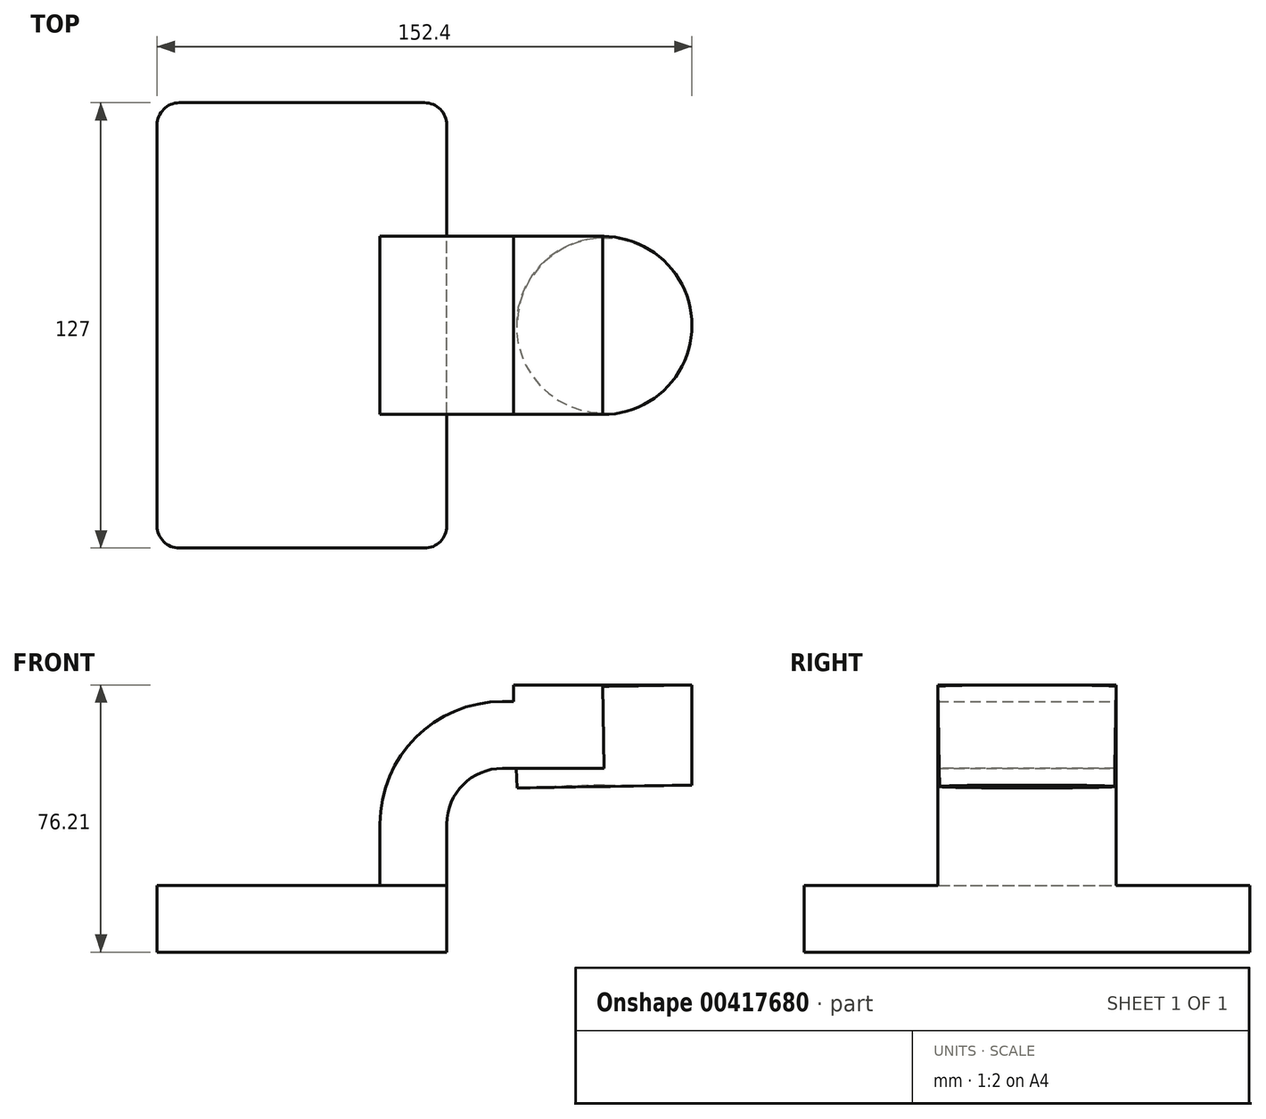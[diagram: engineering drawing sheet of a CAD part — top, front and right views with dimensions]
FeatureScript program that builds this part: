
annotation { "Feature Type Name" : "Feature", "Feature Type Description" : "" }
export const myFeature = defineFeature(function(context is Context, id is Id, definition is map)
    precondition{}
    {
        {
            var Q0;
            Q0=qCreatedBy(makeId("Front.planeOp"),FACE);
            var sketch = newSketch(context, id + "F0", { "sketchPlane" : qUnion([Q0])});
            skLineSegment(sketch, "E0.bottom", {"start": v(41.28, -9.52) * mm, "end": v(-41.27, -9.53) * mm});
            skLineSegment(sketch, "E0.top", {"start": v(41.27, 9.53) * mm, "end": v(-41.28, 9.53) * mm});
            skLineSegment(sketch, "E0.left", {"start": v(41.28, -9.52) * mm, "end": v(41.28, 9.53) * mm});
            skLineSegment(sketch, "E0.right", {"start": v(-41.27, -9.53) * mm, "end": v(-41.28, 9.53) * mm});
            skPoint(sketch, "E0.middle", {"position": v(0, 0) * mm});
            skLineSegment(sketch, "E1.bottom", {"start": v(60.32, 38.1) * mm, "end": v(111.12, 38.1) * mm});
            skLineSegment(sketch, "E1.top", {"start": v(60.32, 66.68) * mm, "end": v(111.12, 66.68) * mm});
            skLineSegment(sketch, "E1.left", {"start": v(60.32, 38.1) * mm, "end": v(60.32, 66.67) * mm});
            skLineSegment(sketch, "E1.right", {"start": v(111.12, 38.1) * mm, "end": v(111.12, 66.67) * mm});
            skPoint(sketch, "E1.middle", {"position": v(85.72, 52.39) * mm});
            skLineSegment(sketch, "E2", {"start": v(41.27, 9.53) * mm, "end": v(41.27, 27) * mm});
            skArc(sketch, "E3", {"start": v(41.27, 27) * mm, "mid": v(45.92, 38.23) * mm, "end": v(57.15, 42.88) * mm});
            skLineSegment(sketch, "E4", {"start": v(57.15, 42.88) * mm, "end": v(86.2, 42.88) * mm});
            skLineSegment(sketch, "E5.0", {"start": v(57.15, 61.93) * mm, "end": v(85.72, 61.93) * mm});
            skArc(sketch, "E5.1", {"start": v(22.23, 27) * mm, "mid": v(32.45, 51.7) * mm, "end": v(57.15, 61.93) * mm});
            skLineSegment(sketch, "E5.2", {"start": v(22.22, 9.53) * mm, "end": v(22.22, 27) * mm});
            skPoint(sketch, "E6", {"position": v(85.72, 66.68) * mm});
            skLineSegment(sketch, "E7", {"start": v(85.72, 66.68) * mm, "end": v(86.2, 38.1) * mm});
            skFitSpline(sketch, "E8", {"points": [v(-41.28, 9.52) * mm, v(57.15, 61.93) * mm], "startDerivative": vector(0.7, 129.9) * mm, "endDerivative": vector(128.03, 0.11) * mm});
            skSolve(sketch);
        }
        {
            var Q0;
            Q0=makeQuery(id+"F0.imprint","IMPRINT",FACE,{"disambiguationData":[TD([[makeQuery(id+"F0.imprint","IMPRINT",EDGE,{"derivedFrom":sQuery(id+"F0.wireOp",EDGE,"E0.bottom")}),-1.0]])]});
            extrude(context, id + "F1", {"entities" : qUnion([Q0]), "endBound" : BoundingType.SYMMETRIC, "depth" : 127 * mm});
        }
        {
            var Q0;
            {var subQ1=sQuery(id+"F0.wireOp",EDGE,"E2");Q0=makeQuery(id+"F0.imprint","IMPRINT",FACE,{"disambiguationData":[TD([[makeQuery(id+"F0.imprint","IMPRINT",EDGE,{"derivedFrom":subQ1}),1.0]])]});}
            var Q1;
            {var subQ1=sQuery(id+"F0.wireOp",EDGE,"E1.left");var subQ5=sQuery(id+"F0.wireOp",EDGE,"E1.top");var subQ6=makeQuery(id+"F0.imprint","INTERSECT",VERTEX,{"derivedFrom":[subQ5,subQ1]});Q1=makeQuery(id+"F0.imprint","IMPRINT",FACE,{"disambiguationData":[TD([[makeQuery(id+"F0.imprint","IMPRINT",EDGE,{"disambiguationData":[TD([[subQ6,-1.0]])],"derivedFrom":subQ5}),-1.0]])]});}
            extrude(context, id + "F2", {"entities" : qUnion([Q0, Q1]), "operationType" : NewBodyOperationType.ADD, "endBound" : BoundingType.SYMMETRIC, "depth" : 50.8 * mm});
        }
        {
            var Q0;
            {var subQ4=sQuery(id+"F0.wireOp",EDGE,"E5.1");Q0=makeQuery(id+"F0.imprint","IMPRINT",FACE,{"disambiguationData":[TD([[makeQuery(id+"F0.imprint","IMPRINT",EDGE,{"derivedFrom":subQ4}),1.0]])]});}
            extrude(context, id + "F3", {"entities" : qUnion([Q0]), "operationType" : NewBodyOperationType.ADD, "endBound" : BoundingType.SYMMETRIC, "depth" : 15.88 * mm});
        }
        {
            var Q0;
            {var subQ4=sQuery(id+"F0.wireOp",EDGE,"E1.right");Q0=makeQuery(id+"F0.imprint","IMPRINT",FACE,{"disambiguationData":[TD([[makeQuery(id+"F0.imprint","IMPRINT",EDGE,{"derivedFrom":subQ4}),1.0]])]});}
            var Q1;
            Q1=sQuery(id+"F0.wireOp",EDGE,"E7");
            revolve(context, id + "F4", {"operationType" : NewBodyOperationType.ADD, "entities" : qUnion([Q0]), "axis" : qUnion([Q1]), "revolveType" : RevolveType.FULL});
        }
        {
            var Q0;
            Q0=makeQuery(id+"F1.opExtrude","CAP_EDGE",EDGE,{"disambiguationData":[OSD([sQuery(id+"F0.wireOp",EDGE,"E0.left")])],"isStart":false});
            var Q1;
            Q1=makeQuery(id+"F1.opExtrude","CAP_EDGE",EDGE,{"disambiguationData":[OSD([sQuery(id+"F0.wireOp",EDGE,"E0.right")])],"isStart":false});
            var Q2;
            Q2=makeQuery(id+"F1.opExtrude","CAP_EDGE",EDGE,{"disambiguationData":[OSD([sQuery(id+"F0.wireOp",EDGE,"E0.left")])],"isStart":true});
            var Q3;
            Q3=makeQuery(id+"F1.opExtrude","CAP_EDGE",EDGE,{"disambiguationData":[OSD([sQuery(id+"F0.wireOp",EDGE,"E0.right")])],"isStart":true});
            fillet(context, id + "F5", {"entities" : qUnion([Q0, Q1, Q2, Q3]), "radius" : 6.35 * mm, "tangentPropagation" : true, "allowEdgeOverflow" : false});
        }
    });
